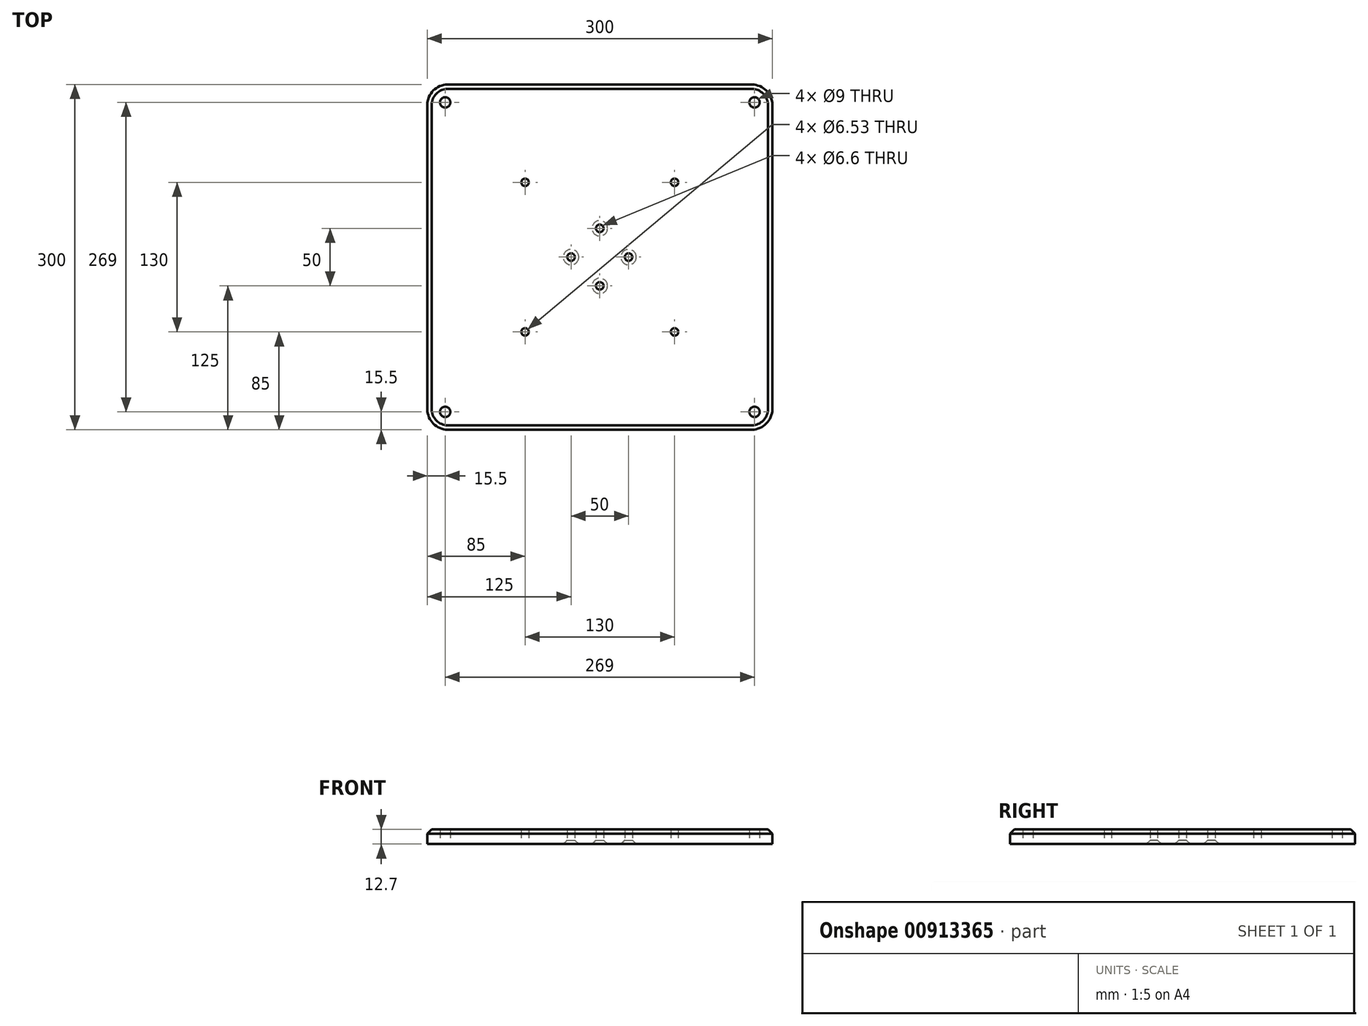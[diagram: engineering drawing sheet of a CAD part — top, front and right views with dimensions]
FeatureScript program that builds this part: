
annotation { "Feature Type Name" : "Feature", "Feature Type Description" : "" }
export const myFeature = defineFeature(function(context is Context, id is Id, definition is map)
    precondition{}
    {
        {
            var Q0;
            Q0=qCreatedBy(makeId("Top.planeOp"),FACE);
            var sketch = newSketch(context, id + "F0", { "sketchPlane" : qUnion([Q0])});
            skLineSegment(sketch, "E0.bottom", {"start": v(150, 150) * mm, "end": v(-150, 150) * mm});
            skLineSegment(sketch, "E0.top", {"start": v(150, -150) * mm, "end": v(-150, -150) * mm});
            skLineSegment(sketch, "E0.left", {"start": v(150, 150) * mm, "end": v(150, -150) * mm});
            skLineSegment(sketch, "E0.right", {"start": v(-150, 150) * mm, "end": v(-150, -150) * mm});
            skPoint(sketch, "E0.middle", {"position": v(0, 0) * mm});
            skSolve(sketch);
        }
        {
            var Q0;
            Q0 = qSketchRegion(id + "F0", true);
            extrude(context, id + "F1", {"entities" : qUnion([Q0]), "depth" : 12.7 * mm, "offsetDistance" : 25.4 * mm});
        }
        {
            var Q0;
            Q0=makeQuery(id+"F1.opExtrude","SWEPT_EDGE",EDGE,{"disambiguationData":[OSD([sQuery(id+"F0.wireOp",EDGE,"E0.top"),sQuery(id+"F0.wireOp",EDGE,"E0.right")])]});
            var Q1;
            Q1=makeQuery(id+"F1.opExtrude","SWEPT_EDGE",EDGE,{"disambiguationData":[OSD([sQuery(id+"F0.wireOp",EDGE,"E0.top"),sQuery(id+"F0.wireOp",EDGE,"E0.left")])]});
            var Q2;
            Q2=makeQuery(id+"F1.opExtrude","SWEPT_EDGE",EDGE,{"disambiguationData":[OSD([sQuery(id+"F0.wireOp",EDGE,"E0.bottom"),sQuery(id+"F0.wireOp",EDGE,"E0.left")])]});
            var Q3;
            Q3=makeQuery(id+"F1.opExtrude","SWEPT_EDGE",EDGE,{"disambiguationData":[OSD([sQuery(id+"F0.wireOp",EDGE,"E0.bottom"),sQuery(id+"F0.wireOp",EDGE,"E0.right")])]});
            var Q4;
            Q4=makeQuery(id+"F3.opChamfer","BLEND_EDGE",EDGE,{"blendedFrom":[makeQuery(id+"F1.opExtrude","CAP_EDGE",EDGE,{"disambiguationData":[OSD([sQuery(id+"F0.wireOp",EDGE,"E0.top")])],"isStart":false}),makeQuery(id+"F1.opExtrude","CAP_EDGE",EDGE,{"disambiguationData":[OSD([sQuery(id+"F0.wireOp",EDGE,"E0.right")])],"isStart":false})],"blendedInto":[]});
            var Q5;
            Q5=makeQuery(id+"F3.opChamfer","BLEND_EDGE",EDGE,{"blendedFrom":[makeQuery(id+"F1.opExtrude","CAP_EDGE",EDGE,{"disambiguationData":[OSD([sQuery(id+"F0.wireOp",EDGE,"E0.top")])],"isStart":false}),makeQuery(id+"F1.opExtrude","CAP_EDGE",EDGE,{"disambiguationData":[OSD([sQuery(id+"F0.wireOp",EDGE,"E0.left")])],"isStart":false})],"blendedInto":[]});
            var Q6;
            Q6=makeQuery(id+"F3.opChamfer","BLEND_EDGE",EDGE,{"blendedFrom":[makeQuery(id+"F1.opExtrude","CAP_EDGE",EDGE,{"disambiguationData":[OSD([sQuery(id+"F0.wireOp",EDGE,"E0.bottom")])],"isStart":false}),makeQuery(id+"F1.opExtrude","CAP_EDGE",EDGE,{"disambiguationData":[OSD([sQuery(id+"F0.wireOp",EDGE,"E0.left")])],"isStart":false})],"blendedInto":[]});
            var Q7;
            Q7=makeQuery(id+"F3.opChamfer","BLEND_EDGE",EDGE,{"blendedFrom":[makeQuery(id+"F1.opExtrude","CAP_EDGE",EDGE,{"disambiguationData":[OSD([sQuery(id+"F0.wireOp",EDGE,"E0.bottom")])],"isStart":false}),makeQuery(id+"F1.opExtrude","CAP_EDGE",EDGE,{"disambiguationData":[OSD([sQuery(id+"F0.wireOp",EDGE,"E0.right")])],"isStart":false})],"blendedInto":[]});
            fillet(context, id + "F2", {"entities" : qUnion([Q0, Q1, Q2, Q3, Q4, Q5, Q6, Q7]), "radius" : 17.78 * mm, "tangentPropagation" : true, "allowEdgeOverflow" : false});
        }
        {
            var Q0;
            Q0=makeQuery(id+"F1.opExtrude","CAP_EDGE",EDGE,{"disambiguationData":[OSD([sQuery(id+"F0.wireOp",EDGE,"E0.right")])],"isStart":false});
            var Q1;
            Q1=makeQuery(id+"F1.opExtrude","CAP_EDGE",EDGE,{"disambiguationData":[OSD([sQuery(id+"F0.wireOp",EDGE,"E0.bottom")])],"isStart":false});
            var Q2;
            Q2=makeQuery(id+"F1.opExtrude","CAP_EDGE",EDGE,{"disambiguationData":[OSD([sQuery(id+"F0.wireOp",EDGE,"E0.left")])],"isStart":false});
            var Q3;
            Q3=makeQuery(id+"F1.opExtrude","CAP_EDGE",EDGE,{"disambiguationData":[OSD([sQuery(id+"F0.wireOp",EDGE,"E0.top")])],"isStart":false});
            chamfer(context, id + "F3", {"entities" : qUnion([Q0, Q1, Q2, Q3]), "width" : 3.8 * mm, "tangentPropagation" : true});
        }
        {
            var Q0;
            Q0=makeQuery(id+"F1.opExtrude","CAP_FACE",FACE,{"disambiguationData":[OSD([sQuery(id+"F0.wireOp",EDGE,"E0.bottom"),sQuery(id+"F0.wireOp",EDGE,"E0.top"),sQuery(id+"F0.wireOp",EDGE,"E0.left"),sQuery(id+"F0.wireOp",EDGE,"E0.right")])],"isStart":true});
            var sketch = newSketch(context, id + "F4", { "sketchPlane" : qUnion([Q0])});
            skPoint(sketch, "E1", {"position": v(-134.5, 134.5) * mm});
            skPoint(sketch, "E2", {"position": v(134.5, 134.5) * mm});
            skPoint(sketch, "E3", {"position": v(134.5, -134.5) * mm});
            skPoint(sketch, "E4", {"position": v(-134.5, -134.5) * mm});
            skSolve(sketch);
        }
        {
            var Q0;
            Q0=sQuery(id+"F4.wireOp",VERTEX,"E1");
            var Q1;
            Q1=sQuery(id+"F4.wireOp",VERTEX,"E2");
            var Q2;
            Q2=sQuery(id+"F4.wireOp",VERTEX,"E4");
            var Q3;
            Q3=sQuery(id+"F4.wireOp",VERTEX,"E3");
            var Q4;
            Q4=makeQuery(id+"F1.opExtrude","SWEPT_BODY",BODY,{"disambiguationData":[OSD([sQuery(id+"F0.wireOp",EDGE,"E0.bottom"),sQuery(id+"F0.wireOp",EDGE,"E0.top"),sQuery(id+"F0.wireOp",EDGE,"E0.left"),sQuery(id+"F0.wireOp",EDGE,"E0.right")])]});
            hole(context, id + "F5", {"style" : HoleStyle.SIMPLE, "endStyle" : HoleEndStyle.THROUGH, "holeDiameter" : 9 * mm, "majorDiameter" : 6.35 * mm, "isTappedThrough" : true, "tappedDepth" : 12.7 * mm, "tapClearance" : 3, "startFromSketch" : true, "locations" : qUnion([Q0, Q1, Q2, Q3]), "scope" : qUnion([Q4])});
        }
        {
            var Q0;
            Q0=makeQuery(id+"F1.opExtrude","CAP_FACE",FACE,{"disambiguationData":[OSD([sQuery(id+"F0.wireOp",EDGE,"E0.bottom"),sQuery(id+"F0.wireOp",EDGE,"E0.top"),sQuery(id+"F0.wireOp",EDGE,"E0.left"),sQuery(id+"F0.wireOp",EDGE,"E0.right")])],"isStart":true});
            var sketch = newSketch(context, id + "F6", { "sketchPlane" : qUnion([Q0])});
            skPoint(sketch, "E5", {"position": v(-65, 65) * mm});
            skPoint(sketch, "E6", {"position": v(65, 65) * mm});
            skPoint(sketch, "E7", {"position": v(65, -65) * mm});
            skPoint(sketch, "E8", {"position": v(-65, -65) * mm});
            skSolve(sketch);
        }
        {
            var Q0;
            Q0=sQuery(id+"F6.wireOp",VERTEX,"E5");
            var Q1;
            Q1=sQuery(id+"F6.wireOp",VERTEX,"E6");
            var Q2;
            Q2=sQuery(id+"F6.wireOp",VERTEX,"E7");
            var Q3;
            Q3=sQuery(id+"F6.wireOp",VERTEX,"E8");
            var Q4;
            Q4=makeQuery(id+"F1.opExtrude","SWEPT_BODY",BODY,{"disambiguationData":[OSD([sQuery(id+"F0.wireOp",EDGE,"E0.bottom"),sQuery(id+"F0.wireOp",EDGE,"E0.top"),sQuery(id+"F0.wireOp",EDGE,"E0.left"),sQuery(id+"F0.wireOp",EDGE,"E0.right")])]});
            hole(context, id + "F7", {"style" : HoleStyle.SIMPLE, "endStyle" : HoleEndStyle.THROUGH, "standardTappedOrClearance" : lookupTablePath({ "standard" : "ANSI", "engagement" : "75%", "pitch" : "18 tpi", "size" : "5/16", "type" : "Tapped" }), "standardBlindInLast" : lookupTablePath({ "standard" : "ANSI", "engagement" : "75%", "pitch" : "18 tpi", "size" : "5/16", "type" : "Tapped" }), "holeDiameter" : 6.53 * mm, "majorDiameter" : 7.94 * mm, "showTappedDepth" : true, "isTappedThrough" : true, "tappedDepth" : 12.7 * mm, "tapClearance" : 3, "startFromSketch" : true, "locations" : qUnion([Q0, Q1, Q2, Q3]), "scope" : qUnion([Q4])});
        }
        {
            var Q0;
            Q0=makeQuery(id+"F1.opExtrude","CAP_FACE",FACE,{"disambiguationData":[OSD([sQuery(id+"F0.wireOp",EDGE,"E0.bottom"),sQuery(id+"F0.wireOp",EDGE,"E0.top"),sQuery(id+"F0.wireOp",EDGE,"E0.left"),sQuery(id+"F0.wireOp",EDGE,"E0.right")])],"isStart":true});
            var sketch = newSketch(context, id + "F8", { "sketchPlane" : qUnion([Q0])});
            skPoint(sketch, "E9", {"position": v(0, 25) * mm});
            skPoint(sketch, "E10", {"position": v(25, 0) * mm});
            skPoint(sketch, "E11", {"position": v(0, -25) * mm});
            skPoint(sketch, "E12", {"position": v(-25, 0) * mm});
            skLineSegment(sketch, "E13", {"start": v(-65, 65) * mm, "end": v(65, 65) * mm, "construction": true});
            skLineSegment(sketch, "E14", {"start": v(-65, 65) * mm, "end": v(-65, -65) * mm, "construction": true});
            skLineSegment(sketch, "E15", {"start": v(-65, -65) * mm, "end": v(65, -65) * mm, "construction": true});
            skLineSegment(sketch, "E16", {"start": v(65, -65) * mm, "end": v(65, 65) * mm, "construction": true});
            skSolve(sketch);
        }
        {
            var Q0;
            Q0=sQuery(id+"F8.wireOp",VERTEX,"E9");
            var Q1;
            Q1=sQuery(id+"F8.wireOp",VERTEX,"E10");
            var Q2;
            Q2=sQuery(id+"F8.wireOp",VERTEX,"E11");
            var Q3;
            Q3=sQuery(id+"F8.wireOp",VERTEX,"E12");
            var Q4;
            Q4=makeQuery(id+"F1.opExtrude","SWEPT_BODY",BODY,{"disambiguationData":[OSD([sQuery(id+"F0.wireOp",EDGE,"E0.bottom"),sQuery(id+"F0.wireOp",EDGE,"E0.top"),sQuery(id+"F0.wireOp",EDGE,"E0.left"),sQuery(id+"F0.wireOp",EDGE,"E0.right")])]});
            hole(context, id + "F9", {"style" : HoleStyle.C_SINK, "endStyle" : HoleEndStyle.THROUGH, "standardTappedOrClearance" : lookupTablePath({ "fit" : "Normal", "standard" : "ISO", "size" : "M6", "type" : "Clearance" }), "standardBlindInLast" : lookupTablePath({ "fit" : "Normal", "standard" : "ISO", "size" : "M6", "type" : "Clearance" }), "holeDiameter" : 6.6 * mm, "cSinkDiameter" : 13.44 * mm, "cSinkAngle" : 90 * degree, "majorDiameter" : 5 * mm, "isTappedThrough" : true, "tappedDepth" : 12.7 * mm, "tapClearance" : 3, "startFromSketch" : true, "locations" : qUnion([Q0, Q1, Q2, Q3]), "scope" : qUnion([Q4])});
        }
    });
